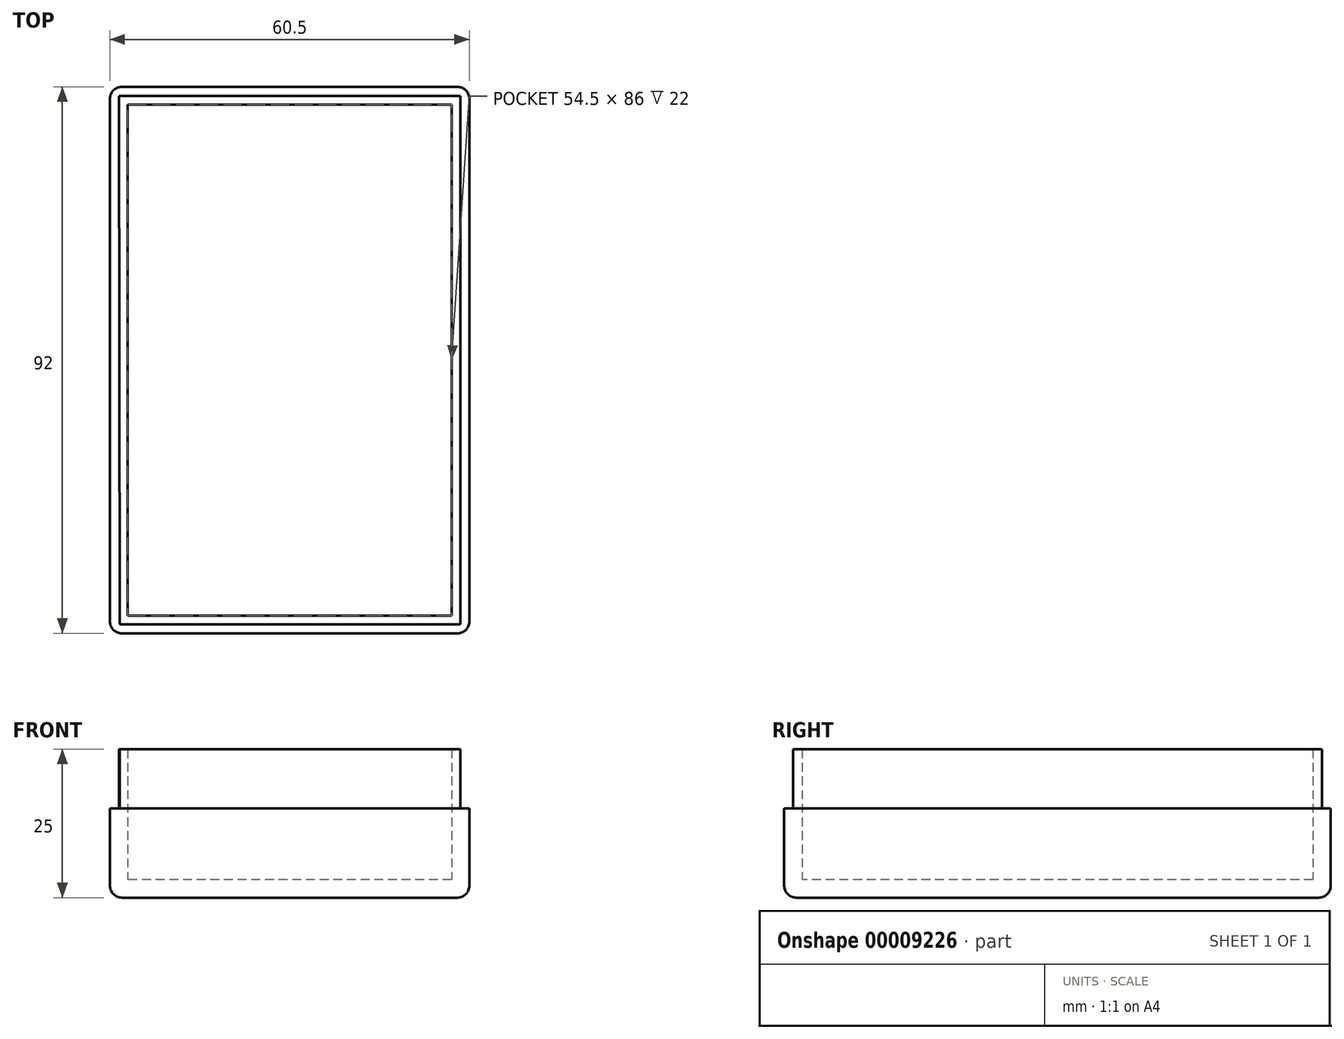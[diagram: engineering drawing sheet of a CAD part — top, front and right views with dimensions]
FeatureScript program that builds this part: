
annotation { "Feature Type Name" : "Feature", "Feature Type Description" : "" }
export const myFeature = defineFeature(function(context is Context, id is Id, definition is map)
    precondition{}
    {
        {
            var Q0;
            Q0=qCreatedBy(makeId("Top.planeOp"),FACE);
            var sketch = newSketch(context, id + "F0", { "sketchPlane" : qUnion([Q0])});
            skLineSegment(sketch, "E0.rect.bottom", {"start": v(30.25, 46) * mm, "end": v(-30.25, 46) * mm});
            skLineSegment(sketch, "E0.rect.top", {"start": v(30.25, -46) * mm, "end": v(-30.25, -46) * mm});
            skLineSegment(sketch, "E0.rect.left", {"start": v(30.25, 46) * mm, "end": v(30.25, -46) * mm});
            skLineSegment(sketch, "E0.rect.right", {"start": v(-30.25, 46) * mm, "end": v(-30.25, -46) * mm});
            skPoint(sketch, "E0.rect.middle", {"position": v(0, 0) * mm});
            skSolve(sketch);
        }
        {
            var Q0;
            Q0=makeQuery(id+"F0.imprint","IMPRINT",FACE,{"disambiguationData":[TD([[makeQuery(id+"F0.imprint","IMPRINT",EDGE,{"derivedFrom":sQuery(id+"F0.wireOp",EDGE,"E0.rect.bottom")}),1.0]])]});
            extrude(context, id + "F1", {"entities" : qUnion([Q0]), "depth" : 25 * mm});
        }
        {
            var Q0;
            Q0=makeQuery(id+"F1.opExtrude","CAP_FACE",FACE,{"disambiguationData":[OSD([sQuery(id+"F0.wireOp",EDGE,"E0.rect.bottom"),sQuery(id+"F0.wireOp",EDGE,"E0.rect.top"),sQuery(id+"F0.wireOp",EDGE,"E0.rect.left"),sQuery(id+"F0.wireOp",EDGE,"E0.rect.right")])],"isStart":false});
            shell(context, id + "F2", {"entities" : qUnion([Q0]), "thickness" : 3 * mm});
        }
        {
            var Q0;
            Q0=makeQuery(id+"F1.opExtrude","CAP_FACE",FACE,{"disambiguationData":[OSD([sQuery(id+"F0.wireOp",EDGE,"E0.rect.bottom"),sQuery(id+"F0.wireOp",EDGE,"E0.rect.top"),sQuery(id+"F0.wireOp",EDGE,"E0.rect.left"),sQuery(id+"F0.wireOp",EDGE,"E0.rect.right")])],"isStart":false});
            var sketch = newSketch(context, id + "F3", { "sketchPlane" : qUnion([Q0])});
            skLineSegment(sketch, "E1", {"start": v(-30.25, 46) * mm, "end": v(30.25, 46) * mm});
            skLineSegment(sketch, "E2", {"start": v(30.25, 46) * mm, "end": v(30.25, -46) * mm});
            skLineSegment(sketch, "E3", {"start": v(30.25, -46) * mm, "end": v(-30.25, -46) * mm});
            skLineSegment(sketch, "E4", {"start": v(-30.25, -46) * mm, "end": v(-30.25, 46) * mm});
            skLineSegment(sketch, "E5", {"start": v(-28.75, 44.5) * mm, "end": v(28.75, 44.5) * mm});
            skLineSegment(sketch, "E6", {"start": v(28.75, 44.5) * mm, "end": v(28.75, -44.5) * mm});
            skLineSegment(sketch, "E7", {"start": v(28.75, -44.5) * mm, "end": v(-28.63, -44.5) * mm});
            skLineSegment(sketch, "E8", {"start": v(-28.63, -44.5) * mm, "end": v(-28.75, 44.5) * mm});
            skSolve(sketch);
        }
        {
            var Q0;
            Q0=makeQuery(id+"F3.imprint","IMPRINT",FACE,{"disambiguationData":[TD([[makeQuery(id+"F3.imprint","IMPRINT",EDGE,{"derivedFrom":sQuery(id+"F3.wireOp",EDGE,"E1")}),1.0]])]});
            extrude(context, id + "F4", {"entities" : qUnion([Q0]), "operationType" : NewBodyOperationType.REMOVE, "oppositeDirection" : true, "depth" : 10 * mm});
        }
        {
            var Q0;
            Q0=makeQuery(id+"F1.opExtrude","SWEPT_EDGE",EDGE,{"disambiguationData":[OSD([sQuery(id+"F0.wireOp",EDGE,"E0.rect.top"),sQuery(id+"F0.wireOp",EDGE,"E0.rect.left")])]});
            var Q1;
            Q1=makeQuery(id+"F1.opExtrude","SWEPT_EDGE",EDGE,{"disambiguationData":[OSD([sQuery(id+"F0.wireOp",EDGE,"E0.rect.top"),sQuery(id+"F0.wireOp",EDGE,"E0.rect.right")])]});
            var Q2;
            Q2=makeQuery(id+"F1.opExtrude","SWEPT_EDGE",EDGE,{"disambiguationData":[OSD([sQuery(id+"F0.wireOp",EDGE,"E0.rect.bottom"),sQuery(id+"F0.wireOp",EDGE,"E0.rect.left")])]});
            var Q3;
            Q3=makeQuery(id+"F1.opExtrude","SWEPT_EDGE",EDGE,{"disambiguationData":[OSD([sQuery(id+"F0.wireOp",EDGE,"E0.rect.bottom"),sQuery(id+"F0.wireOp",EDGE,"E0.rect.right")])]});
            var Q4;
            Q4=makeQuery(id+"F1.opExtrude","CAP_EDGE",EDGE,{"disambiguationData":[OSD([sQuery(id+"F0.wireOp",EDGE,"E0.rect.bottom")])],"isStart":true});
            var Q5;
            Q5=makeQuery(id+"F1.opExtrude","CAP_EDGE",EDGE,{"disambiguationData":[OSD([sQuery(id+"F0.wireOp",EDGE,"E0.rect.left")])],"isStart":true});
            var Q6;
            Q6=makeQuery(id+"F1.opExtrude","CAP_EDGE",EDGE,{"disambiguationData":[OSD([sQuery(id+"F0.wireOp",EDGE,"E0.rect.top")])],"isStart":true});
            var Q7;
            Q7=makeQuery(id+"F1.opExtrude","CAP_EDGE",EDGE,{"disambiguationData":[OSD([sQuery(id+"F0.wireOp",EDGE,"E0.rect.right")])],"isStart":true});
            fillet(context, id + "F5", {"entities" : qUnion([Q0, Q1, Q2, Q3, Q4, Q5, Q6, Q7]), "radius" : 2 * mm, "tangentPropagation" : true, "allowEdgeOverflow" : false});
        }
    });
